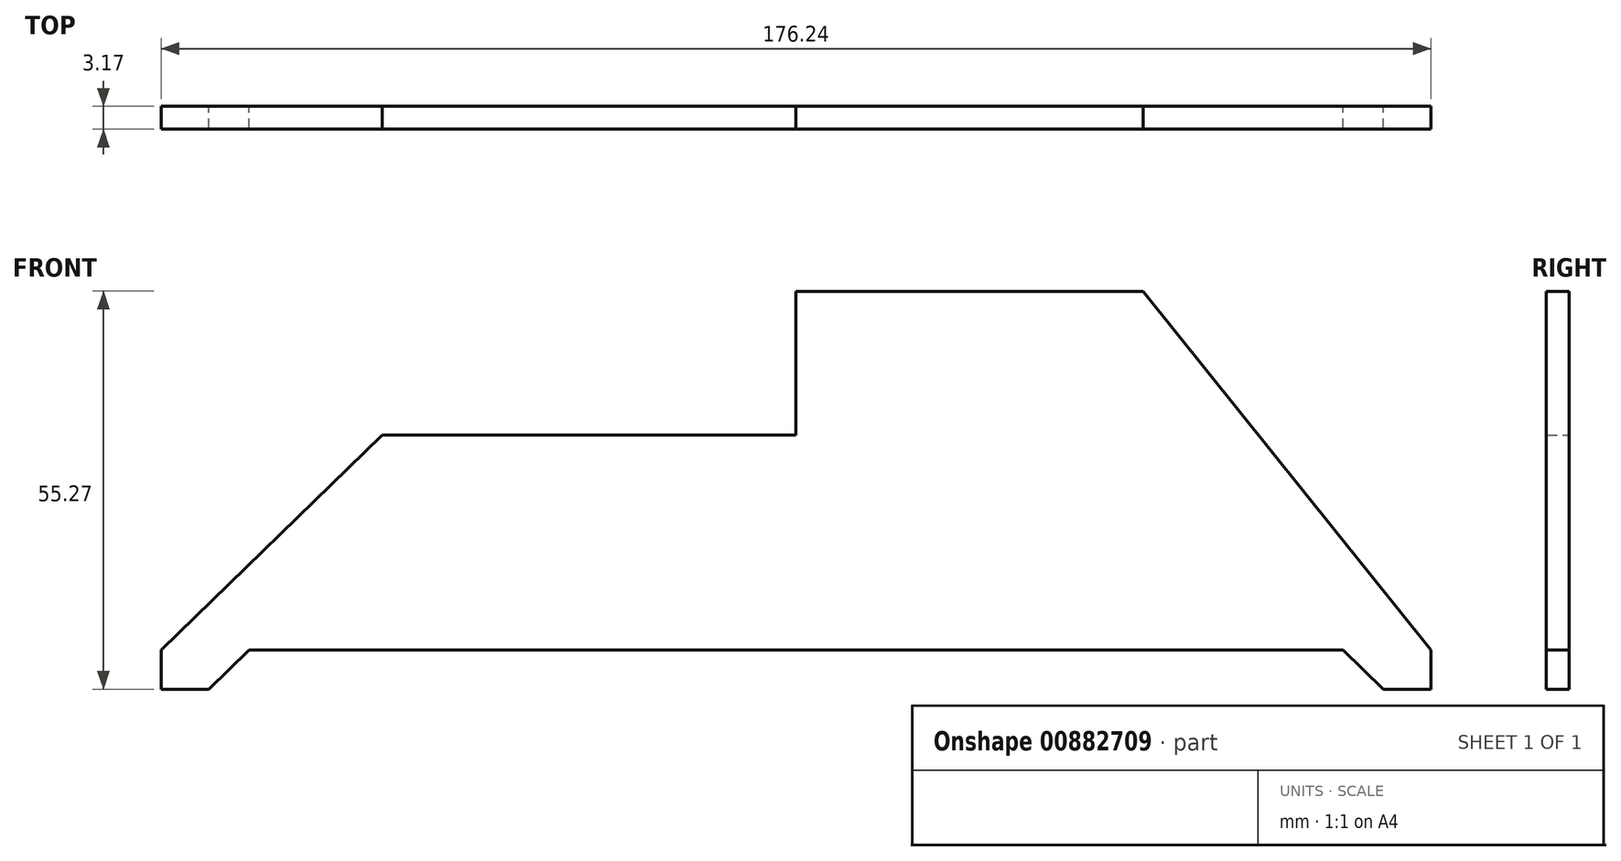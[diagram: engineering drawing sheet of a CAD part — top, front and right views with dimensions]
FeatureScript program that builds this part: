
annotation { "Feature Type Name" : "Feature", "Feature Type Description" : "" }
export const myFeature = defineFeature(function(context is Context, id is Id, definition is map)
    precondition{}
    {
        {
            var Q0;
            Q0=qCreatedBy(makeId("Front.planeOp"),FACE);
            var sketch = newSketch(context, id + "F0", { "sketchPlane" : qUnion([Q0])});
            skLineSegment(sketch, "E0", {"start": v(-75.9, 0) * mm, "end": v(0, 0) * mm});
            skLineSegment(sketch, "E1", {"start": v(0, 0) * mm, "end": v(0, 29.86) * mm});
            skLineSegment(sketch, "E2", {"start": v(0, 29.86) * mm, "end": v(-57.45, 29.86) * mm});
            skLineSegment(sketch, "E3", {"start": v(-57.45, 29.86) * mm, "end": v(-88.12, 0) * mm});
            skLineSegment(sketch, "E4", {"start": v(-88.12, 0) * mm, "end": v(-88.12, -5.44) * mm});
            skLineSegment(sketch, "E5", {"start": v(-88.12, -5.44) * mm, "end": v(-81.5, -5.44) * mm});
            skLineSegment(sketch, "E6", {"start": v(-81.5, -5.44) * mm, "end": v(-75.9, 0) * mm});
            skLineSegment(sketch, "E7.MirrorCS", {"start": v(75.9, 0) * mm, "end": v(0, 0) * mm});
            skLineSegment(sketch, "E8.MirrorCS", {"start": v(81.5, -5.44) * mm, "end": v(75.9, 0) * mm});
            skLineSegment(sketch, "E9.MirrorCS", {"start": v(88.12, -5.44) * mm, "end": v(81.5, -5.44) * mm});
            skLineSegment(sketch, "E10.MirrorCS", {"start": v(88.12, 0) * mm, "end": v(88.12, -5.44) * mm});
            skLineSegment(sketch, "E11", {"start": v(0, 29.86) * mm, "end": v(0, 49.83) * mm});
            skLineSegment(sketch, "E12", {"start": v(0, 49.83) * mm, "end": v(48.2, 49.83) * mm});
            skLineSegment(sketch, "E13", {"start": v(48.2, 49.83) * mm, "end": v(88.12, 0) * mm});
            skLineSegment(sketch, "E14", {"start": v(24.1, 49.83) * mm, "end": v(24.1, 0) * mm});
            skLineSegment(sketch, "E15", {"start": v(-28.73, 29.86) * mm, "end": v(-28.73, 0) * mm});
            skSolve(sketch);
        }
        {
            var Q0;
            Q0 = qSketchRegion(id + "F0", true);
            extrude(context, id + "F1", {"entities" : qUnion([Q0]), "depth" : 3.17 * mm, "offsetDistance" : 25.4 * mm});
        }
    });
